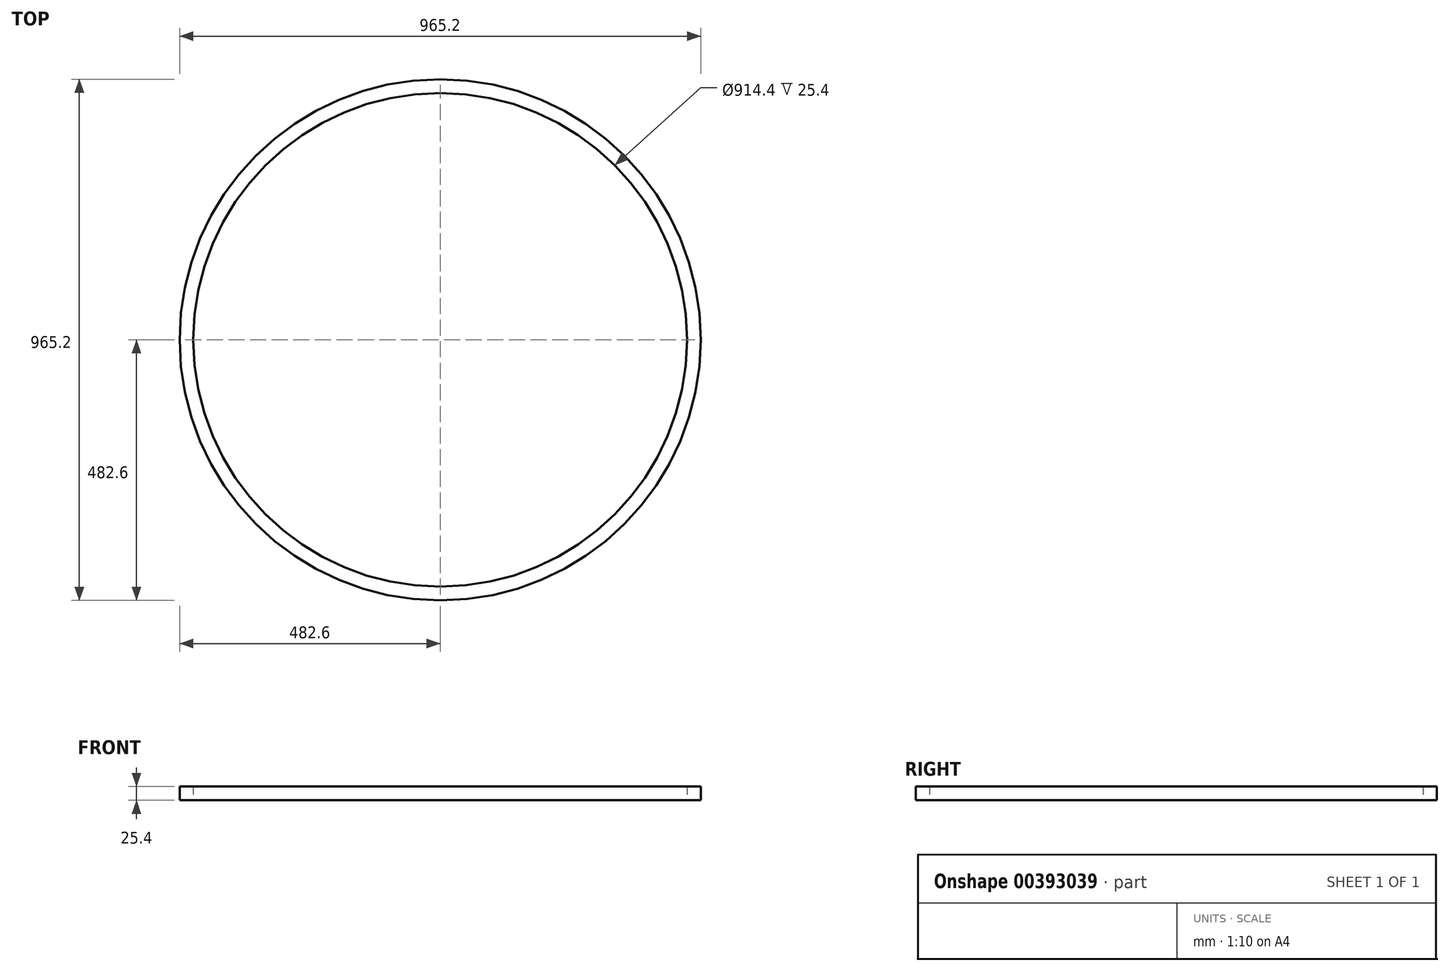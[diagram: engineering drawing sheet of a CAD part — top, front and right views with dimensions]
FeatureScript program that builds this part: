
annotation { "Feature Type Name" : "Feature", "Feature Type Description" : "" }
export const myFeature = defineFeature(function(context is Context, id is Id, definition is map)
    precondition{}
    {
        {
            var Q0;
            Q0=qCreatedBy(makeId("Top.planeOp"),FACE);
            var sketch = newSketch(context, id + "F0", { "sketchPlane" : qUnion([Q0])});
            skCircle(sketch, "E0", {"center": v(0, 0) * mm, "radius": 457.2 * mm});
            skCircle(sketch, "E1", {"center": v(0, 0) * mm, "radius": 482.6 * mm});
            skSolve(sketch);
        }
        {
            var Q0;
            Q0 = qSketchRegion(id + "F0", true);
            extrude(context, id + "F1", {"entities" : qUnion([Q0]), "depth" : 25.4 * mm});
        }
    });
